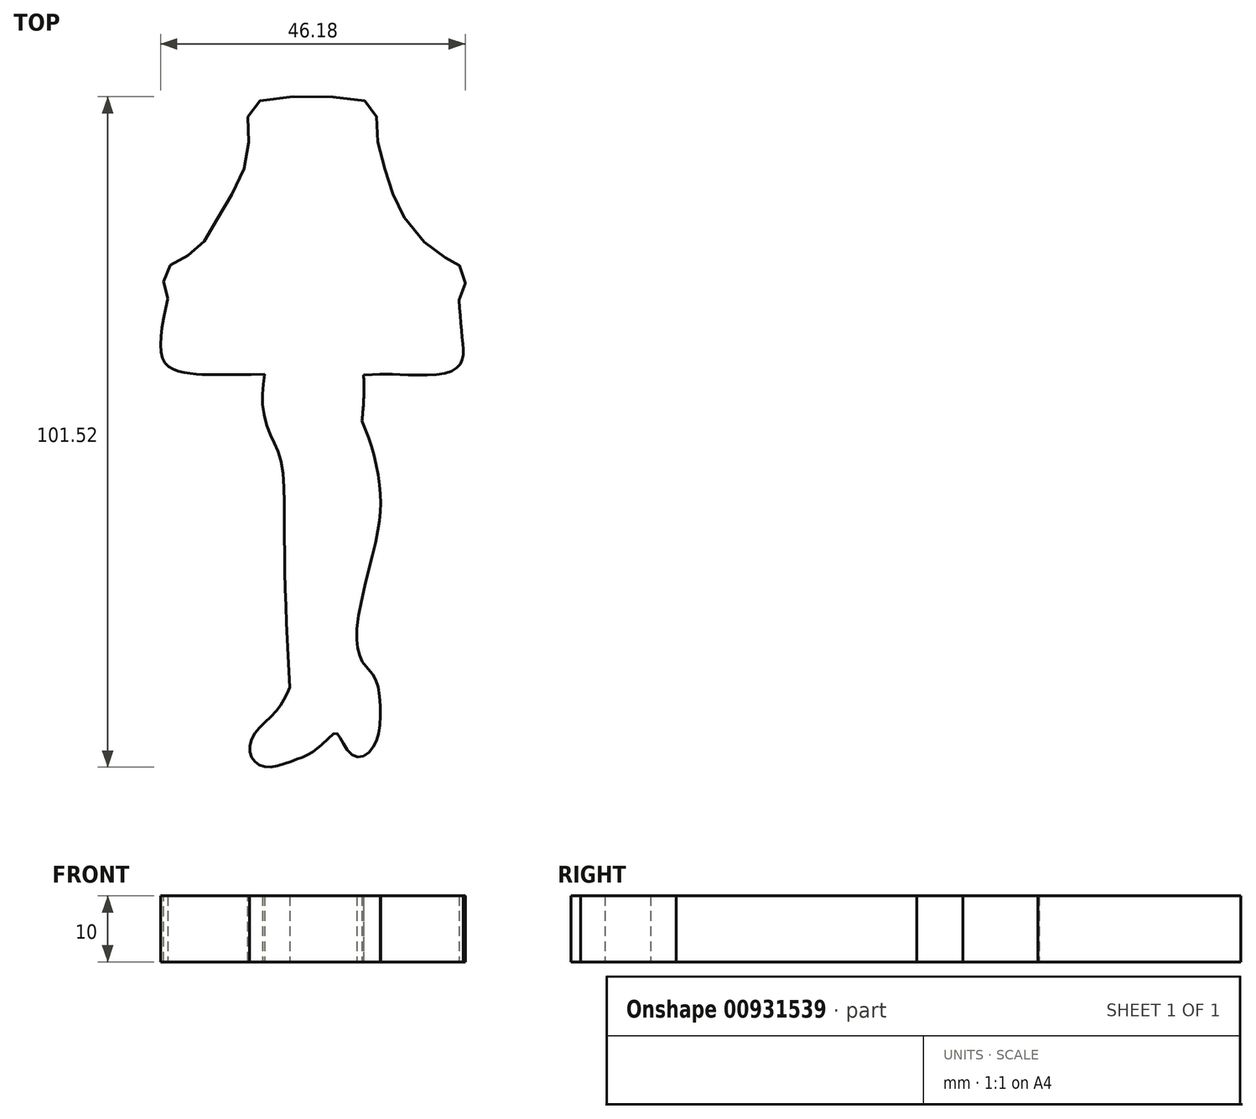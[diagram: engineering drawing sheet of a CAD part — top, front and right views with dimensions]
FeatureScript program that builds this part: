
annotation { "Feature Type Name" : "Feature", "Feature Type Description" : "" }
export const myFeature = defineFeature(function(context is Context, id is Id, definition is map)
    precondition{}
    {
        {
            var Q0;
            Q0=qCreatedBy(makeId("Top.planeOp"),FACE);
            var sketch = newSketch(context, id + "F0", { "sketchPlane" : qUnion([Q0])});
            skFitSpline(sketch, "E0", {"points": [v(-21.96, 21.73) * mm, v(-22.57, 24.53) * mm, v(-21.29, 27.07) * mm, v(-17.78, 28.94) * mm, v(-14.8, 33.22) * mm, v(-11.09, 39.69) * mm, v(-9.68, 46.22) * mm, v(-9.26, 50.92) * mm, v(0.2, 52.32) * mm, v(9.05, 50.98) * mm, v(9.78, 46.46) * mm, v(11.49, 39.69) * mm, v(13.8, 34.08) * mm, v(19.54, 28.22) * mm, v(21.96, 27.07) * mm, v(23.12, 24.24) * mm, v(22.18, 21.55) * mm], "startDerivative": vector(-36.08, 49.2) * mm, "endDerivative": vector(-20.03, -56.15) * mm});
            skFitSpline(sketch, "E1", {"points": [v(-21.96, 21.73) * mm, v(-22.77, 12.75) * mm, v(-20.1, 10.68) * mm, v(-15.6, 10.24) * mm, v(-7.27, 10.28) * mm], "startDerivative": vector(-7.58, -34.1) * mm, "endDerivative": vector(52.45, 0.9) * mm});
            skLineSegment(sketch, "E2", {"start": v(26.4, 27.07) * mm, "end": v(-25.18, 27.07) * mm, "construction": true});
            skLineSegment(sketch, "E3", {"start": v(-23.74, 10.21) * mm, "end": v(30.1, 10.28) * mm, "construction": true});
            skLineSegment(sketch, "E4", {"start": v(0.2, 52.32) * mm, "end": v(1.18, -49.28) * mm, "construction": true});
            skFitSpline(sketch, "E5", {"points": [v(22.18, 21.55) * mm, v(22.66, 15.88) * mm, v(22.7, 12.63) * mm, v(20.81, 10.67) * mm, v(13.05, 10.24) * mm, v(7.69, 10.18) * mm], "startDerivative": vector(1.93, -27.6) * mm, "endDerivative": vector(-35.4, -1.75) * mm});
            skFitSpline(sketch, "E6", {"points": [v(7.69, 10.18) * mm, v(7.48, 3.22) * mm], "startDerivative": vector(0.72, -7.32) * mm, "endDerivative": vector(-0.4, -4.2) * mm});
            skFitSpline(sketch, "E7", {"points": [v(-7.27, 10.28) * mm, v(-7.58, 5.76) * mm, v(-6.37, 1.06) * mm, v(-4.86, -2.57) * mm, v(-4.28, -12.01) * mm, v(-4.05, -25.4) * mm, v(-3.45, -37.1) * mm], "startDerivative": vector(-5.06, -34.24) * mm, "endDerivative": vector(3.4, -55.06) * mm});
            skFitSpline(sketch, "E8", {"points": [v(-3.45, -37.1) * mm, v(-5.6, -40.8) * mm, v(-9.11, -44.65) * mm, v(-9.18, -47.86) * mm, v(-6.84, -49.2) * mm, v(-2.86, -48.19) * mm, v(0.04, -46.9) * mm], "startDerivative": vector(-9.75, -21.66) * mm, "endDerivative": vector(19.62, 13) * mm});
            skFitSpline(sketch, "E9", {"points": [v(0.04, -46.9) * mm, v(3.51, -44.05) * mm, v(4.77, -45.9) * mm, v(6.92, -47.7) * mm, v(9.16, -46.22) * mm, v(10.2, -42.2) * mm, v(9.7, -36.37) * mm, v(7.51, -33.27) * mm], "startDerivative": vector(33.23, 22.12) * mm, "endDerivative": vector(-23.26, 28.95) * mm});
            skFitSpline(sketch, "E10", {"points": [v(7.51, -33.27) * mm, v(6.68, -28.84) * mm, v(9.6, -14.78) * mm, v(10.29, -8.59) * mm, v(9.34, -2.13) * mm, v(7.48, 3.22) * mm], "startDerivative": vector(-8.63, 22.45) * mm, "endDerivative": vector(-11.42, 28.63) * mm});
            skSolve(sketch);
        }
        {
            var Q0;
            Q0 = qSketchRegion(id + "F0", true);
            extrude(context, id + "F1", {"entities" : qUnion([Q0]), "depth" : 2 * mm, "offsetDistance" : 25 * mm});
        }
        {
            var Q0;
            Q0=makeQuery(id+"F1.opExtrude","CAP_FACE",FACE,{"disambiguationData":[OSD([sQuery(id+"F0.wireOp",EDGE,"E0"),sQuery(id+"F0.wireOp",EDGE,"E1"),sQuery(id+"F0.wireOp",EDGE,"E5"),sQuery(id+"F0.wireOp",EDGE,"E6"),sQuery(id+"F0.wireOp",EDGE,"E7"),sQuery(id+"F0.wireOp",EDGE,"E8"),sQuery(id+"F0.wireOp",EDGE,"E9"),sQuery(id+"F0.wireOp",EDGE,"E10")])],"isStart":false});
            extrude(context, id + "F2", {"entities" : qUnion([Q0]), "operationType" : NewBodyOperationType.ADD, "depth" : 8 * mm, "offsetDistance" : 25 * mm});
        }
    });
